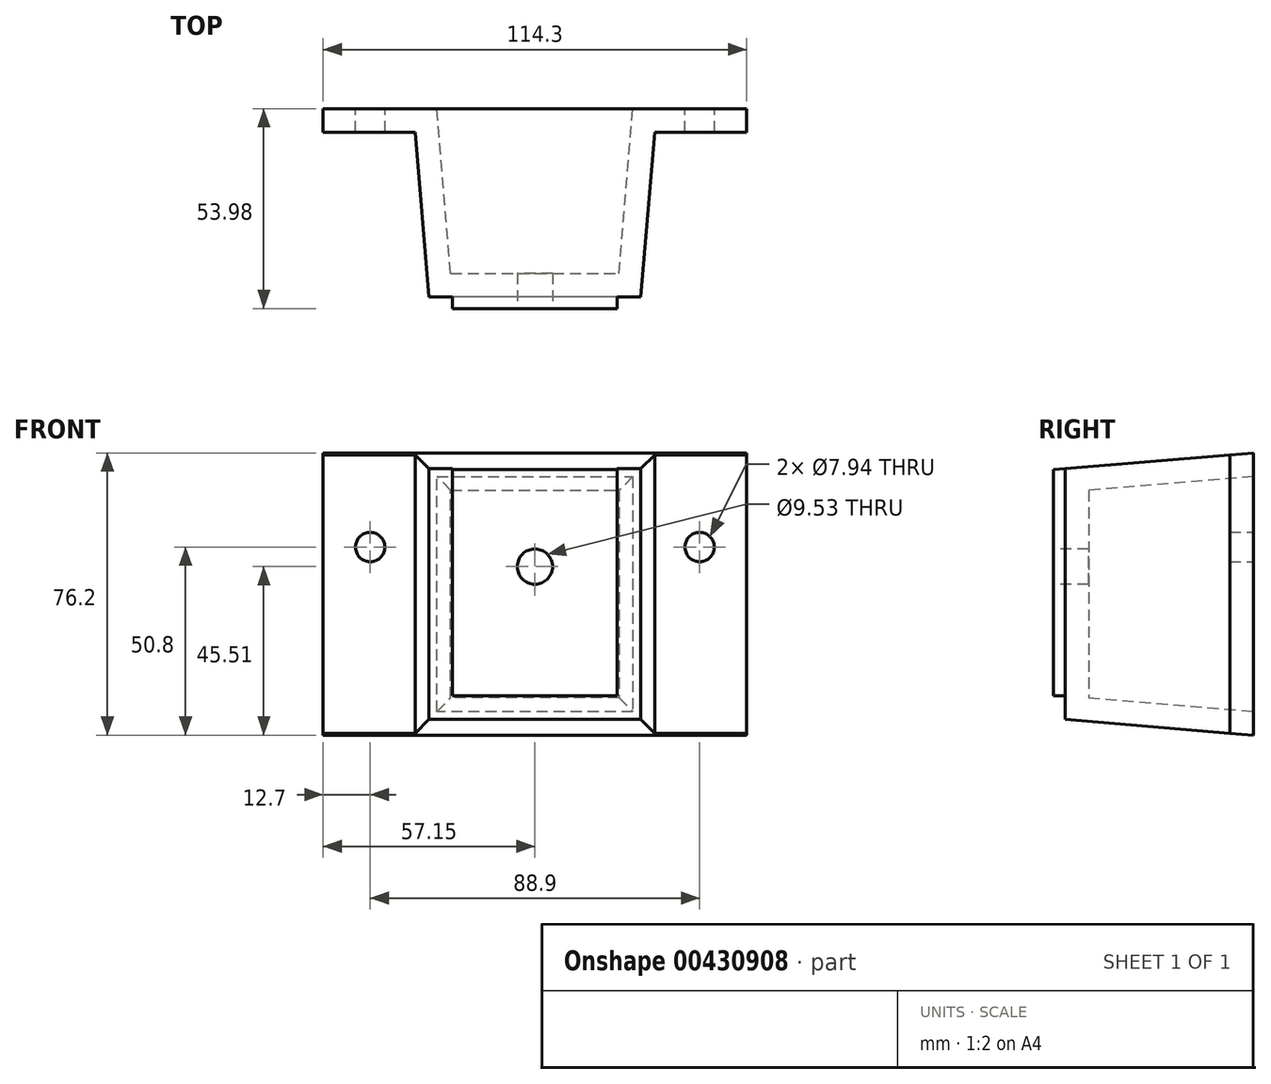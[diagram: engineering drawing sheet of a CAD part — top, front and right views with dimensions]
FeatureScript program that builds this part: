
annotation { "Feature Type Name" : "Feature", "Feature Type Description" : "" }
export const myFeature = defineFeature(function(context is Context, id is Id, definition is map)
    precondition{}
    {
        {
            var Q0;
            Q0=qCreatedBy(makeId("Front.planeOp"),FACE);
            var sketch = newSketch(context, id + "F0", { "sketchPlane" : qUnion([Q0])});
            skLineSegment(sketch, "E0.bottom", {"start": v(32.81, 38.1) * mm, "end": v(-32.81, 38.1) * mm});
            skLineSegment(sketch, "E0.top", {"start": v(32.81, -38.1) * mm, "end": v(-32.81, -38.1) * mm});
            skLineSegment(sketch, "E0.left", {"start": v(32.81, 38.1) * mm, "end": v(32.81, -38.1) * mm});
            skLineSegment(sketch, "E0.right", {"start": v(-32.81, 38.1) * mm, "end": v(-32.81, -38.1) * mm});
            skPoint(sketch, "E0.middle", {"position": v(0, 0) * mm});
            skLineSegment(sketch, "E1", {"start": v(-32.81, 38.1) * mm, "end": v(-32.81, 88.9) * mm, "construction": true});
            skLineSegment(sketch, "E2", {"start": v(-32.81, 88.9) * mm, "end": v(-35.99, 88.9) * mm, "construction": true});
            skLineSegment(sketch, "E3", {"start": v(-35.99, 88.9) * mm, "end": v(-32.81, 38.1) * mm, "construction": true});
            skSolve(sketch);
        }
        {
            var Q0;
            Q0=qSketchRegion(id+"F0",true);
            extrude(context, id + "F1", {"entities" : qUnion([Q0]), "depth" : 50.8 * mm, "hasDraft" : true, "draftAngle" : 4.76 * degree, "draftPullDirection" : true});
        }
        {
            var Q0;
            Q0=makeQuery(id+"F1.opExtrude","CAP_FACE",FACE,{"disambiguationData":[OSD([sQuery(id+"F0.wireOp",EDGE,"E0.bottom"),sQuery(id+"F0.wireOp",EDGE,"E0.top"),sQuery(id+"F0.wireOp",EDGE,"E0.left"),sQuery(id+"F0.wireOp",EDGE,"E0.right")])],"isStart":true});
            shell(context, id + "F2", {"entities" : qUnion([Q0]), "thickness" : 6.35 * mm});
        }
        {
            var Q0;
            Q0=makeQuery(id+"F1.opExtrude","CAP_FACE",FACE,{"disambiguationData":[OSD([sQuery(id+"F0.wireOp",EDGE,"E0.bottom"),sQuery(id+"F0.wireOp",EDGE,"E0.top"),sQuery(id+"F0.wireOp",EDGE,"E0.left"),sQuery(id+"F0.wireOp",EDGE,"E0.right")])],"isStart":false});
            var sketch = newSketch(context, id + "F3", { "sketchPlane" : qUnion([Q0])});
            skLineSegment(sketch, "E4.0", {"start": v(22.23, 33.87) * mm, "end": v(22.23, -27.52) * mm});
            skLineSegment(sketch, "E4.1", {"start": v(22.23, -27.52) * mm, "end": v(-22.23, -27.52) * mm});
            skLineSegment(sketch, "E4.2", {"start": v(-22.23, 33.87) * mm, "end": v(-22.23, -27.52) * mm});
            skLineSegment(sketch, "E5.0.0", {"start": v(-28.58, -33.87) * mm, "end": v(28.58, -33.87) * mm});
            skLineSegment(sketch, "E5.0.1", {"start": v(28.58, -33.87) * mm, "end": v(28.58, 33.87) * mm});
            skLineSegment(sketch, "E5.0.2", {"start": v(28.58, 33.87) * mm, "end": v(-28.58, 33.87) * mm});
            skLineSegment(sketch, "E5.0.3", {"start": v(-28.58, 33.87) * mm, "end": v(-28.58, -33.87) * mm});
            skSolve(sketch);
        }
        {
            var Q0;
            {var subQ0=sQuery(id+"F3.wireOp",EDGE,"E4.0");Q0=makeQuery(id+"F3.imprint","IMPRINT",FACE,{"disambiguationData":[TD([[makeQuery(id+"F3.imprint","IMPRINT",EDGE,{"derivedFrom":subQ0}),-1.0]])]});}
            extrude(context, id + "F4", {"entities" : qUnion([Q0]), "operationType" : NewBodyOperationType.ADD, "depth" : 3.17 * mm});
        }
        {
            var Q0;
            Q0=qCreatedBy(makeId("Front.planeOp"),FACE);
            var sketch = newSketch(context, id + "F5", { "sketchPlane" : qUnion([Q0])});
            skLineSegment(sketch, "E6.0", {"start": v(26.44, -31.73) * mm, "end": v(-26.44, -31.73) * mm});
            skLineSegment(sketch, "E7.0", {"start": v(26.44, 31.73) * mm, "end": v(26.44, -31.73) * mm});
            skLineSegment(sketch, "E8.0", {"start": v(26.44, 31.73) * mm, "end": v(-26.44, 31.73) * mm});
            skLineSegment(sketch, "E9.0", {"start": v(-26.44, 31.73) * mm, "end": v(-26.44, -31.73) * mm});
            skLineSegment(sketch, "E10.0", {"start": v(32.81, -38.1) * mm, "end": v(-32.81, -38.1) * mm});
            skLineSegment(sketch, "E11.0", {"start": v(32.81, 38.1) * mm, "end": v(-32.81, 38.1) * mm});
            skLineSegment(sketch, "E12.bottom", {"start": v(57.15, -38.1) * mm, "end": v(-57.15, -38.1) * mm});
            skLineSegment(sketch, "E12.top", {"start": v(57.15, 38.1) * mm, "end": v(-57.15, 38.1) * mm});
            skLineSegment(sketch, "E12.left", {"start": v(57.15, -38.1) * mm, "end": v(57.15, 38.1) * mm});
            skLineSegment(sketch, "E12.right", {"start": v(-57.15, -38.1) * mm, "end": v(-57.15, 38.1) * mm});
            skPoint(sketch, "E12.middle", {"position": v(0, 0) * mm});
            skSolve(sketch);
        }
        {
            var Q0;
            Q0=makeQuery(id+"F5.imprint","IMPRINT",FACE,{"disambiguationData":[TD([[makeQuery(id+"F5.imprint","IMPRINT",EDGE,{"derivedFrom":sQuery(id+"F5.wireOp",EDGE,"E6.0")}),1.0]])]});
            extrude(context, id + "F6", {"entities" : qUnion([Q0]), "operationType" : NewBodyOperationType.ADD, "depth" : 6.35 * mm});
        }
        {
            var Q0;
            Q0=makeQuery(id+"F1.opExtrude","SWEPT_FACE",FACE,{"disambiguationData":[OSD([sQuery(id+"F0.wireOp",EDGE,"E0.bottom")])]});
            var sketch = newSketch(context, id + "F7", { "sketchPlane" : qUnion([Q0])});
            skCircle(sketch, "E13", {"center": v(28.58, -47.81) * mm, "radius": 127 * mm});
            skSolve(sketch);
        }
        {
            var Q0;
            Q0=qSketchRegion(id+"F7",true);
            extrude(context, id + "F8", {"entities" : qUnion([Q0]), "operationType" : NewBodyOperationType.REMOVE, "endBound" : BoundingType.THROUGH_ALL, "depth" : 25.4 * mm});
        }
        {
            var Q0;
            Q0=makeQuery(id+"F1.opExtrude","SWEPT_FACE",FACE,{"disambiguationData":[OSD([sQuery(id+"F0.wireOp",EDGE,"E0.top")])]});
            var sketch = newSketch(context, id + "F9", { "sketchPlane" : qUnion([Q0])});
            skCircle(sketch, "E14", {"center": v(-28.58, 47.81) * mm, "radius": 114.3 * mm});
            skSolve(sketch);
        }
        {
            var Q0;
            Q0=qSketchRegion(id+"F9",true);
            extrude(context, id + "F10", {"entities" : qUnion([Q0]), "operationType" : NewBodyOperationType.REMOVE, "endBound" : BoundingType.THROUGH_ALL, "depth" : 25.4 * mm});
        }
        {
            var Q0;
            Q0=makeQuery(id+"F6.boolean.opBoolean","MERGE",FACE,{"derivedFrom":[makeQuery(id+"F1.opExtrude","CAP_FACE",FACE,{"disambiguationData":[OSD([sQuery(id+"F0.wireOp",EDGE,"E0.bottom"),sQuery(id+"F0.wireOp",EDGE,"E0.top"),sQuery(id+"F0.wireOp",EDGE,"E0.left"),sQuery(id+"F0.wireOp",EDGE,"E0.right")])],"isStart":true}),makeQuery(id+"F6.opExtrude","CAP_FACE",FACE,{"disambiguationData":[OSD([sQuery(id+"F5.wireOp",EDGE,"E6.0"),sQuery(id+"F5.wireOp",EDGE,"E7.0"),sQuery(id+"F5.wireOp",EDGE,"E8.0"),sQuery(id+"F5.wireOp",EDGE,"E9.0"),sQuery(id+"F5.wireOp",EDGE,"E12.bottom"),sQuery(id+"F5.wireOp",EDGE,"E12.top"),sQuery(id+"F5.wireOp",EDGE,"E12.left"),sQuery(id+"F5.wireOp",EDGE,"E12.right")])],"isStart":true})]});
            var sketch = newSketch(context, id + "F11", { "sketchPlane" : qUnion([Q0])});
            skCircle(sketch, "E15", {"center": v(-44.45, 12.7) * mm, "radius": 3.97 * mm});
            skCircle(sketch, "E16", {"center": v(44.45, 12.7) * mm, "radius": 3.97 * mm});
            skSolve(sketch);
        }
        {
            var Q0;
            Q0=qSketchRegion(id+"F11",true);
            extrude(context, id + "F12", {"entities" : qUnion([Q0]), "operationType" : NewBodyOperationType.REMOVE, "endBound" : BoundingType.THROUGH_ALL, "oppositeDirection" : true, "depth" : 25.4 * mm});
        }
        {
            var Q0;
            Q0=makeQuery(id+"F4.opExtrude","CAP_FACE",FACE,{"disambiguationData":[OSD([sQuery(id+"F3.wireOp",EDGE,"E4.0"),sQuery(id+"F3.wireOp",EDGE,"E4.1"),sQuery(id+"F3.wireOp",EDGE,"E4.2"),sQuery(id+"F3.wireOp",EDGE,"E5.0.2")])],"isStart":false});
            var sketch = newSketch(context, id + "F13", { "sketchPlane" : qUnion([Q0])});
            skCircle(sketch, "E17", {"center": v(0, 7.4) * mm, "radius": 4.76 * mm});
            skLineSegment(sketch, "E18.0", {"start": v(28.58, -33.87) * mm, "end": v(-28.58, -33.87) * mm});
            skLineSegment(sketch, "E19", {"start": v(0, -27.52) * mm, "end": v(0, 7.4) * mm, "construction": true});
            skSolve(sketch);
        }
        {
            var Q0;
            Q0=qSketchRegion(id+"F13",true);
            extrude(context, id + "F14", {"entities" : qUnion([Q0]), "operationType" : NewBodyOperationType.REMOVE, "endBound" : BoundingType.THROUGH_ALL, "oppositeDirection" : true, "depth" : 25.4 * mm});
        }
    });
